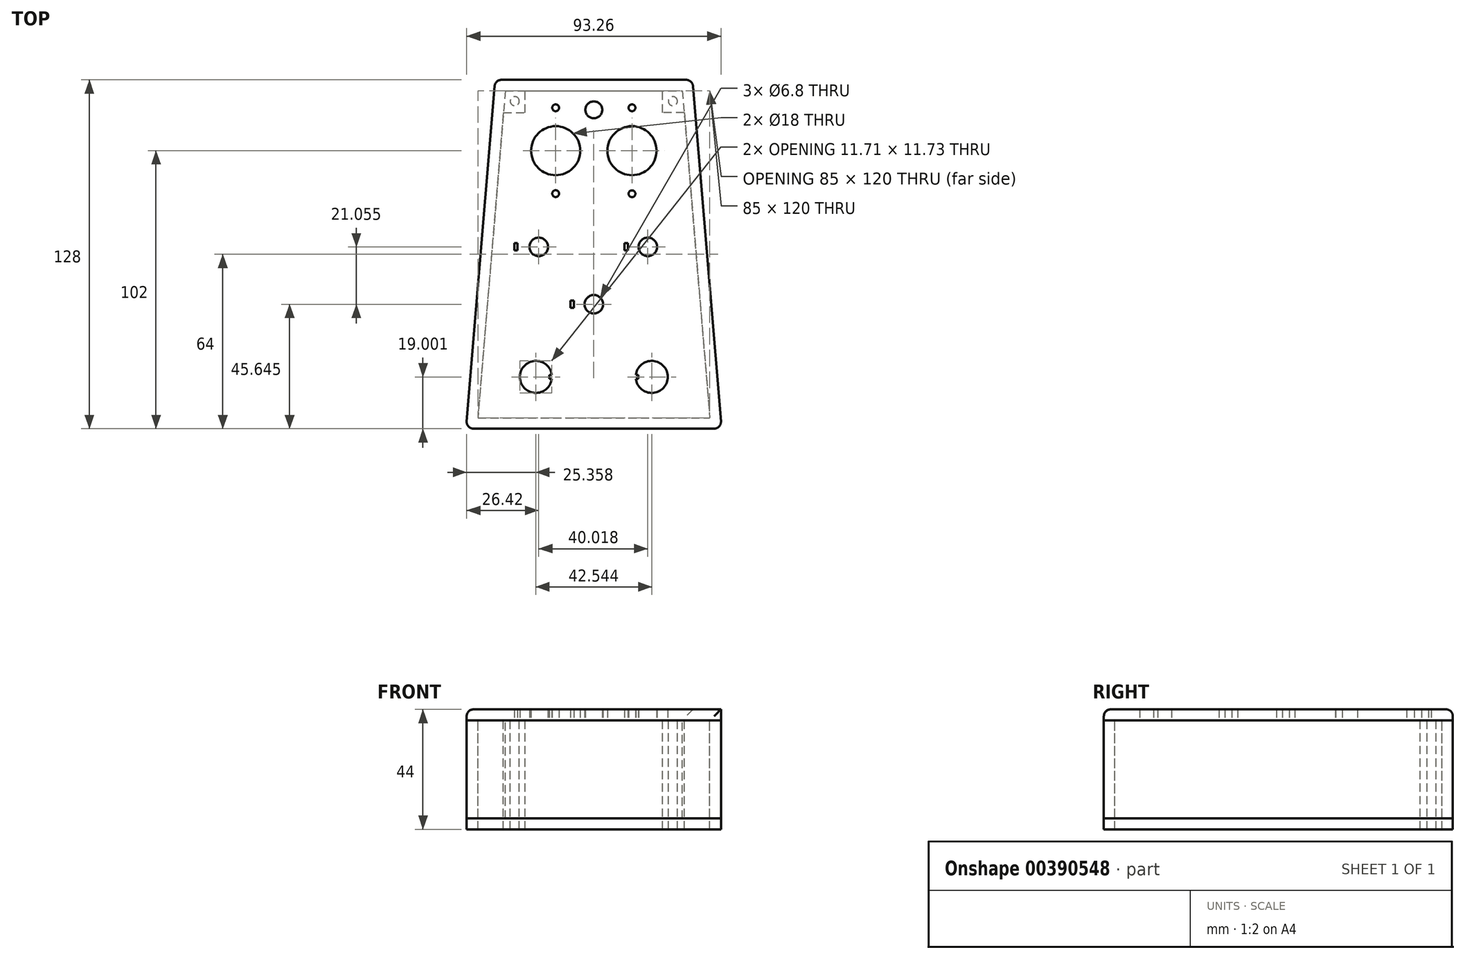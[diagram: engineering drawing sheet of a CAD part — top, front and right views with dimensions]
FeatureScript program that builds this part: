
annotation { "Feature Type Name" : "Feature", "Feature Type Description" : "" }
export const myFeature = defineFeature(function(context is Context, id is Id, definition is map)
    precondition{}
    {
        {
            var Q0;
            Q0=qCreatedBy(makeId("Top.planeOp"),FACE);
            var sketch = newSketch(context, id + "F0", { "sketchPlane" : qUnion([Q0])});
            skLineSegment(sketch, "E0", {"start": v(0, 0) * mm, "end": v(42.5, 0) * mm});
            skLineSegment(sketch, "E1", {"start": v(0, 0) * mm, "end": v(-42.5, 0) * mm});
            skLineSegment(sketch, "E2", {"start": v(-32.5, 120) * mm, "end": v(-42.5, 0) * mm});
            skLineSegment(sketch, "E3", {"start": v(32.5, 120) * mm, "end": v(42.5, 0) * mm});
            skCircle(sketch, "E4", {"center": v(14, 98) * mm, "radius": 9 * mm});
            skCircle(sketch, "E5", {"center": v(-14, 98) * mm, "radius": 9 * mm});
            skCircle(sketch, "E6", {"center": v(-14, 113.75) * mm, "radius": 1.25 * mm});
            skCircle(sketch, "E7", {"center": v(14, 113.75) * mm, "radius": 1.25 * mm});
            skCircle(sketch, "E8.MirrorC", {"center": v(14, 82.2) * mm, "radius": 1.25 * mm});
            skCircle(sketch, "E9.MirrorC", {"center": v(-14, 82.25) * mm, "radius": 1.25 * mm});
            skCircle(sketch, "E10", {"center": v(0, 113) * mm, "radius": 3.1 * mm});
            skLineSegment(sketch, "E11", {"start": v(-46.85, -4) * mm, "end": v(46.85, -4) * mm});
            skLineSegment(sketch, "E12", {"start": v(36.18, 124) * mm, "end": v(46.85, -4) * mm});
            skLineSegment(sketch, "E13", {"start": v(36.18, 124) * mm, "end": v(-36.18, 124) * mm});
            skLineSegment(sketch, "E14", {"start": v(-46.85, -4) * mm, "end": v(-36.18, 124) * mm});
            skLineSegment(sketch, "E15", {"start": v(0, -4) * mm, "end": v(-46.85, -4) * mm});
            skLineSegment(sketch, "E16", {"start": v(46.85, -4) * mm, "end": v(36.18, 124) * mm});
            skLineSegment(sketch, "E17", {"start": v(-36.18, 124) * mm, "end": v(0, 124) * mm});
            skLineSegment(sketch, "E18", {"start": v(-32.5, 120) * mm, "end": v(32.5, 120) * mm});
            skLineSegment(sketch, "E19", {"start": v(-33.17, 112) * mm, "end": v(-25.17, 112) * mm});
            skLineSegment(sketch, "E20", {"start": v(33.17, 112) * mm, "end": v(25.17, 112) * mm});
            skLineSegment(sketch, "E21", {"start": v(25.17, 112) * mm, "end": v(25.17, 120) * mm});
            skLineSegment(sketch, "E22", {"start": v(-25.17, 112) * mm, "end": v(-25.17, 120) * mm});
            skCircle(sketch, "E23", {"center": v(-29, 116.17) * mm, "radius": 1.68 * mm});
            skCircle(sketch, "E24", {"center": v(29, 116.17) * mm, "radius": 1.68 * mm});
            skPoint(sketch, "E25", {"position": v(41.25, 15) * mm});
            skPoint(sketch, "E26", {"position": v(-41.25, 15) * mm});
            skPoint(sketch, "E27", {"position": v(-21.25, 15) * mm});
            skPoint(sketch, "E28", {"position": v(21.25, 15) * mm});
            skArc(sketch, "E29", {"start": v(-15.42, 15.72) * mm, "mid": v(-27.12, 15.01) * mm, "end": v(-15.42, 14.26) * mm});
            skCircle(sketch, "E30", {"center": v(-21.25, 15) * mm, "radius": 14.5 * mm, "construction": true});
            skCircle(sketch, "E31", {"center": v(19.8, 62.7) * mm, "radius": 3.4 * mm});
            skCircle(sketch, "E32", {"center": v(-20.21, 62.7) * mm, "radius": 3.4 * mm});
            skCircle(sketch, "E33", {"center": v(-20.21, 62.7) * mm, "radius": 12.25 * mm, "construction": true});
            skCircle(sketch, "E34", {"center": v(19.8, 62.7) * mm, "radius": 12.25 * mm, "construction": true});
            skPoint(sketch, "E35", {"position": v(0, 41.64) * mm});
            skCircle(sketch, "E36", {"center": v(0, 41.64) * mm, "radius": 12.25 * mm, "construction": true});
            skCircle(sketch, "E37", {"center": v(0, 41.64) * mm, "radius": 3.4 * mm});
            skLineSegment(sketch, "E38", {"start": v(-16.38, 15) * mm, "end": v(-16.38, 15.72) * mm});
            skLineSegment(sketch, "E39", {"start": v(-16.38, 15.72) * mm, "end": v(-15.42, 15.72) * mm});
            skLineSegment(sketch, "E40", {"start": v(-16.38, 15) * mm, "end": v(-16.38, 14.26) * mm});
            skLineSegment(sketch, "E41", {"start": v(-16.38, 14.26) * mm, "end": v(-15.42, 14.26) * mm});
            skPoint(sketch, "E42", {"position": v(-15.42, 15.72) * mm});
            skPoint(sketch, "E43", {"position": v(-15.42, 14.26) * mm});
            skCircle(sketch, "E44.MirrorC", {"center": v(21.25, 15) * mm, "radius": 14.5 * mm, "construction": true});
            skArc(sketch, "E45.MirrorCS", {"start": v(15.42, 15.72) * mm, "mid": v(27.12, 15.01) * mm, "end": v(15.42, 14.26) * mm});
            skLineSegment(sketch, "E46.MirrorCS", {"start": v(16.38, 15) * mm, "end": v(16.38, 14.26) * mm});
            skLineSegment(sketch, "E47.MirrorCS", {"start": v(16.38, 15) * mm, "end": v(16.38, 15.72) * mm});
            skLineSegment(sketch, "E48.MirrorCS", {"start": v(16.38, 15.72) * mm, "end": v(15.42, 15.72) * mm});
            skLineSegment(sketch, "E49.MirrorCS", {"start": v(16.38, 14.26) * mm, "end": v(15.42, 14.26) * mm});
            skPoint(sketch, "E50.MirrorP", {"position": v(15.42, 15.72) * mm});
            skPoint(sketch, "E51.MirrorP", {"position": v(15.42, 14.26) * mm});
            skLineSegment(sketch, "E52.bottom", {"start": v(-8.53, 42.94) * mm, "end": v(-7.28, 42.94) * mm});
            skLineSegment(sketch, "E52.top", {"start": v(-8.53, 40.34) * mm, "end": v(-7.28, 40.34) * mm});
            skLineSegment(sketch, "E52.left", {"start": v(-8.53, 42.94) * mm, "end": v(-8.53, 40.34) * mm});
            skLineSegment(sketch, "E52.right", {"start": v(-7.28, 42.94) * mm, "end": v(-7.28, 40.34) * mm});
            skLineSegment(sketch, "E53.bottom", {"start": v(11.23, 64.07) * mm, "end": v(12.48, 64.07) * mm});
            skLineSegment(sketch, "E53.top", {"start": v(11.23, 61.47) * mm, "end": v(12.48, 61.47) * mm});
            skLineSegment(sketch, "E53.left", {"start": v(11.23, 64.07) * mm, "end": v(11.23, 61.47) * mm});
            skLineSegment(sketch, "E53.right", {"start": v(12.48, 64.07) * mm, "end": v(12.48, 61.47) * mm});
            skLineSegment(sketch, "E54.MirrorCS", {"start": v(-29.2, 64.07) * mm, "end": v(-29.2, 61.47) * mm});
            skLineSegment(sketch, "E55.MirrorCS", {"start": v(-29.2, 64.07) * mm, "end": v(-27.95, 64.07) * mm});
            skLineSegment(sketch, "E56.MirrorCS", {"start": v(-29.2, 61.47) * mm, "end": v(-27.95, 61.47) * mm});
            skLineSegment(sketch, "E57.MirrorCS", {"start": v(-27.95, 64.07) * mm, "end": v(-27.95, 61.47) * mm});
            skSolve(sketch);
        }
        {
            var Q0;
            {var subQ1=sQuery(id+"F0.wireOp",EDGE,"E0");Q0=makeQuery(id+"F0.imprint","IMPRINT",FACE,{"disambiguationData":[TD([[makeQuery(id+"F0.imprint","IMPRINT",EDGE,{"derivedFrom":subQ1}),-1.0]])]});}
            extrude(context, id + "F1", {"entities" : qUnion([Q0]), "depth" : -36 * mm});
        }
        {
            var Q0;
            {var subQ1=sQuery(id+"F0.wireOp",EDGE,"E19");Q0=makeQuery(id+"F0.imprint","IMPRINT",FACE,{"disambiguationData":[TD([[makeQuery(id+"F0.imprint","IMPRINT",EDGE,{"derivedFrom":subQ1}),1.0]])]});}
            var Q1;
            Q1=makeQuery(id+"F0.imprint","IMPRINT",FACE,{"disambiguationData":[TD([[makeQuery(id+"F0.imprint","IMPRINT",EDGE,{"derivedFrom":sQuery(id+"F0.wireOp",EDGE,"E4")}),-1.0]])]});
            var Q2;
            Q2=makeQuery(id+"F0.imprint","IMPRINT",FACE,{"disambiguationData":[TD([[makeQuery(id+"F0.imprint","IMPRINT",EDGE,{"derivedFrom":sQuery(id+"F0.wireOp",EDGE,"E24")}),1.0]])]});
            var Q3;
            {var subQ4=sQuery(id+"F0.wireOp",EDGE,"E20");Q3=makeQuery(id+"F0.imprint","IMPRINT",FACE,{"disambiguationData":[TD([[makeQuery(id+"F0.imprint","IMPRINT",EDGE,{"derivedFrom":subQ4}),-1.0]])]});}
            var Q4;
            Q4=makeQuery(id+"F0.imprint","IMPRINT",FACE,{"disambiguationData":[TD([[makeQuery(id+"F0.imprint","IMPRINT",EDGE,{"derivedFrom":sQuery(id+"F0.wireOp",EDGE,"E23")}),1.0]])]});
            var Q5;
            {var subQ1=sQuery(id+"F0.wireOp",EDGE,"E0");Q5=makeQuery(id+"F0.imprint","IMPRINT",FACE,{"disambiguationData":[TD([[makeQuery(id+"F0.imprint","IMPRINT",EDGE,{"derivedFrom":subQ1}),1.0]])]});}
            var Q6;
            {var subQ1=sQuery(id+"F0.wireOp",EDGE,"E0");Q6=makeQuery(id+"F0.imprint","IMPRINT",FACE,{"disambiguationData":[TD([[makeQuery(id+"F0.imprint","IMPRINT",EDGE,{"derivedFrom":subQ1}),-1.0]])]});}
            extrude(context, id + "F2", {"entities" : qUnion([Q0, Q1, Q2, Q3, Q4, Q5, Q6]), "depth" : 4 * mm});
        }
        {
            var Q0;
            Q0 = qSketchRegion(id + "F0", true);
            var Q1;
            {var subQ4=sQuery(id+"F0.wireOp",EDGE,"E20");Q1=makeQuery(id+"F0.imprint","IMPRINT",FACE,{"disambiguationData":[TD([[makeQuery(id+"F0.imprint","IMPRINT",EDGE,{"derivedFrom":subQ4}),-1.0]])]});}
            var Q2;
            {var subQ1=sQuery(id+"F0.wireOp",EDGE,"E19");Q2=makeQuery(id+"F0.imprint","IMPRINT",FACE,{"disambiguationData":[TD([[makeQuery(id+"F0.imprint","IMPRINT",EDGE,{"derivedFrom":subQ1}),1.0]])]});}
            extrude(context, id + "F3", {"entities" : qUnion([Q0, Q1, Q2]), "depth" : -40 * mm});
        }
        {
            var Q0;
            Q0=makeQuery(id+"F2.opExtrude","SWEPT_EDGE",EDGE,{"disambiguationData":[OSD([sQuery(id+"F0.wireOp",EDGE,"E14"),sQuery(id+"F0.wireOp",EDGE,"E15")])]});
            var Q1;
            Q1=makeQuery(id+"F3.opExtrude","SWEPT_EDGE",EDGE,{"disambiguationData":[OSD([sQuery(id+"F0.wireOp",EDGE,"E14"),sQuery(id+"F0.wireOp",EDGE,"E15")])]});
            var Q2;
            Q2=makeQuery(id+"F2.opExtrude","SWEPT_EDGE",EDGE,{"disambiguationData":[OSD([sQuery(id+"F0.wireOp",EDGE,"E11"),sQuery(id+"F0.wireOp",EDGE,"E16")])]});
            var Q3;
            Q3=makeQuery(id+"F3.opExtrude","SWEPT_EDGE",EDGE,{"disambiguationData":[OSD([sQuery(id+"F0.wireOp",EDGE,"E11"),sQuery(id+"F0.wireOp",EDGE,"E16")])]});
            var Q4;
            Q4=makeQuery(id+"F2.opExtrude","SWEPT_EDGE",EDGE,{"disambiguationData":[OSD([sQuery(id+"F0.wireOp",EDGE,"E14"),sQuery(id+"F0.wireOp",EDGE,"E17")])]});
            var Q5;
            Q5=makeQuery(id+"F3.opExtrude","SWEPT_EDGE",EDGE,{"disambiguationData":[OSD([sQuery(id+"F0.wireOp",EDGE,"E14"),sQuery(id+"F0.wireOp",EDGE,"E17")])]});
            var Q6;
            Q6=makeQuery(id+"F2.opExtrude","SWEPT_EDGE",EDGE,{"disambiguationData":[OSD([sQuery(id+"F0.wireOp",EDGE,"E13"),sQuery(id+"F0.wireOp",EDGE,"E16")])]});
            var Q7;
            Q7=makeQuery(id+"F3.opExtrude","SWEPT_EDGE",EDGE,{"disambiguationData":[OSD([sQuery(id+"F0.wireOp",EDGE,"E13"),sQuery(id+"F0.wireOp",EDGE,"E16")])]});
            var Q8;
            Q8=makeQuery(id+"F2.opExtrude","CAP_EDGE",EDGE,{"disambiguationData":[OSD([sQuery(id+"F0.wireOp",EDGE,"E13"),sQuery(id+"F0.wireOp",EDGE,"E17")])],"isStart":false});
            var Q9;
            Q9=makeQuery(id+"F2.opExtrude","CAP_EDGE",EDGE,{"disambiguationData":[OSD([sQuery(id+"F0.wireOp",EDGE,"E16")])],"isStart":false});
            var Q10;
            Q10=makeQuery(id+"F2.opExtrude","CAP_EDGE",EDGE,{"disambiguationData":[OSD([sQuery(id+"F0.wireOp",EDGE,"E11"),sQuery(id+"F0.wireOp",EDGE,"E15")])],"isStart":false});
            var Q11;
            Q11=makeQuery(id+"F2.opExtrude","CAP_EDGE",EDGE,{"disambiguationData":[OSD([sQuery(id+"F0.wireOp",EDGE,"E14")])],"isStart":false});
            var Q12;
            Q12=makeQuery(id+"F1.opExtrude","SWEPT_EDGE",EDGE,{"disambiguationData":[OSD([sQuery(id+"F0.wireOp",EDGE,"E14"),sQuery(id+"F0.wireOp",EDGE,"E17")])]});
            var Q13;
            Q13=makeQuery(id+"F1.opExtrude","SWEPT_EDGE",EDGE,{"disambiguationData":[OSD([sQuery(id+"F0.wireOp",EDGE,"E14"),sQuery(id+"F0.wireOp",EDGE,"E15")])]});
            var Q14;
            Q14=makeQuery(id+"F1.opExtrude","SWEPT_EDGE",EDGE,{"disambiguationData":[OSD([sQuery(id+"F0.wireOp",EDGE,"E11"),sQuery(id+"F0.wireOp",EDGE,"E16")])]});
            var Q15;
            Q15=makeQuery(id+"F1.opExtrude","SWEPT_EDGE",EDGE,{"disambiguationData":[OSD([sQuery(id+"F0.wireOp",EDGE,"E13"),sQuery(id+"F0.wireOp",EDGE,"E16")])]});
            fillet(context, id + "F4", {"entities" : qUnion([Q0, Q1, Q2, Q3, Q4, Q5, Q6, Q7, Q8, Q9, Q10, Q11, Q12, Q13, Q14, Q15]), "radius" : 2.5 * mm, "tangentPropagation" : true, "allowEdgeOverflow" : false});
        }
    });
